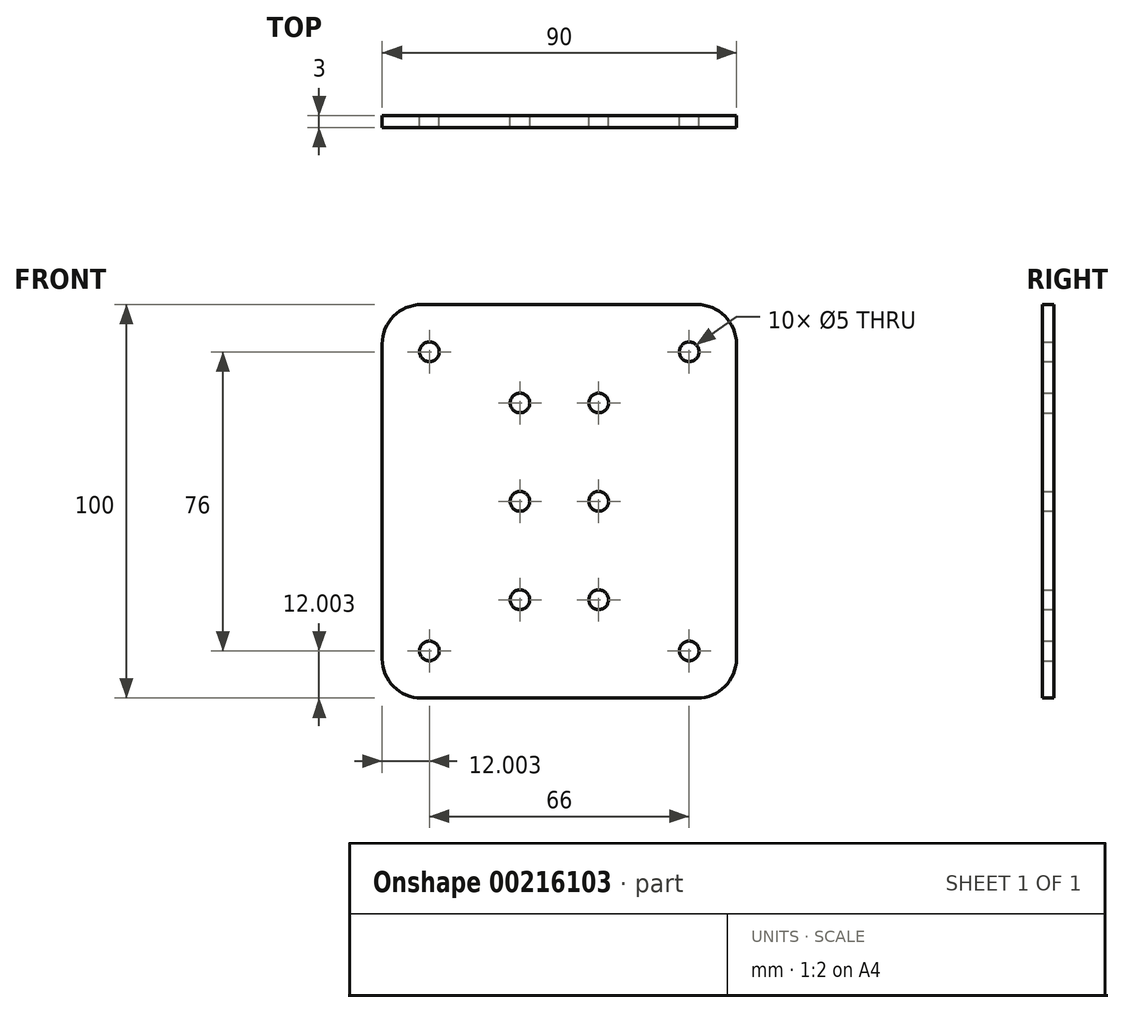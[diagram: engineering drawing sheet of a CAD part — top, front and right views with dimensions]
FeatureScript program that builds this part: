
annotation { "Feature Type Name" : "Feature", "Feature Type Description" : "" }
export const myFeature = defineFeature(function(context is Context, id is Id, definition is map)
    precondition{}
    {
        {
            var Q0;
            Q0=qCreatedBy(makeId("Front.planeOp"),FACE);
            var sketch = newSketch(context, id + "F0", { "sketchPlane" : qUnion([Q0])});
            skLineSegment(sketch, "E0.bottom", {"start": v(-55.35, 70.45) * mm, "end": v(34.65, 70.45) * mm});
            skLineSegment(sketch, "E0.top", {"start": v(-55.35, -29.55) * mm, "end": v(34.65, -29.55) * mm});
            skLineSegment(sketch, "E0.left", {"start": v(-55.35, 70.45) * mm, "end": v(-55.35, -29.55) * mm});
            skLineSegment(sketch, "E0.right", {"start": v(34.65, 70.45) * mm, "end": v(34.65, -29.55) * mm});
            skCircle(sketch, "E1", {"center": v(-43.35, 58.45) * mm, "radius": 2.5 * mm});
            skCircle(sketch, "E2", {"center": v(22.65, 58.45) * mm, "radius": 2.5 * mm});
            skCircle(sketch, "E3", {"center": v(22.65, -17.55) * mm, "radius": 2.5 * mm});
            skCircle(sketch, "E4", {"center": v(-43.35, -17.55) * mm, "radius": 2.5 * mm});
            skCircle(sketch, "E5", {"center": v(-20.35, -4.55) * mm, "radius": 2.5 * mm});
            skCircle(sketch, "E6", {"center": v(-0.35, -4.55) * mm, "radius": 2.5 * mm});
            skCircle(sketch, "E7", {"center": v(-0.35, 20.45) * mm, "radius": 2.5 * mm});
            skCircle(sketch, "E8", {"center": v(-20.35, 20.45) * mm, "radius": 2.5 * mm});
            skCircle(sketch, "E9", {"center": v(-0.35, 45.45) * mm, "radius": 2.5 * mm});
            skCircle(sketch, "E10", {"center": v(-20.35, 45.45) * mm, "radius": 2.5 * mm});
            skLineSegment(sketch, "E11.bottom", {"start": v(-20.35, 45.45) * mm, "end": v(-0.35, 45.45) * mm, "construction": true});
            skLineSegment(sketch, "E11.top", {"start": v(-20.35, -4.55) * mm, "end": v(-0.35, -4.55) * mm, "construction": true});
            skLineSegment(sketch, "E11.left", {"start": v(-20.35, 45.45) * mm, "end": v(-20.35, -4.55) * mm, "construction": true});
            skLineSegment(sketch, "E11.right", {"start": v(-0.35, 45.45) * mm, "end": v(-0.35, -4.55) * mm, "construction": true});
            skSolve(sketch);
        }
        {
            var Q0;
            Q0=makeQuery(id+"F0.imprint","IMPRINT",FACE,{"disambiguationData":[TD([[makeQuery(id+"F0.imprint","IMPRINT",EDGE,{"derivedFrom":sQuery(id+"F0.wireOp",EDGE,"E0.bottom")}),-1.0]])]});
            extrude(context, id + "F1", {"entities" : qUnion([Q0]), "depth" : 3 * mm});
        }
        {
            var Q0;
            Q0=makeQuery(id+"F1.opExtrude","SWEPT_EDGE",EDGE,{"disambiguationData":[OSD([sQuery(id+"F0.wireOp",EDGE,"E0.bottom"),sQuery(id+"F0.wireOp",EDGE,"E0.right")])]});
            var Q1;
            Q1=makeQuery(id+"F1.opExtrude","SWEPT_EDGE",EDGE,{"disambiguationData":[OSD([sQuery(id+"F0.wireOp",EDGE,"E0.bottom"),sQuery(id+"F0.wireOp",EDGE,"E0.left")])]});
            var Q2;
            Q2=makeQuery(id+"F1.opExtrude","SWEPT_EDGE",EDGE,{"disambiguationData":[OSD([sQuery(id+"F0.wireOp",EDGE,"E0.top"),sQuery(id+"F0.wireOp",EDGE,"E0.left")])]});
            var Q3;
            Q3=makeQuery(id+"F1.opExtrude","SWEPT_EDGE",EDGE,{"disambiguationData":[OSD([sQuery(id+"F0.wireOp",EDGE,"E0.top"),sQuery(id+"F0.wireOp",EDGE,"E0.right")])]});
            fillet(context, id + "F2", {"entities" : qUnion([Q0, Q1, Q2, Q3]), "radius" : 10 * mm, "tangentPropagation" : true, "allowEdgeOverflow" : false});
        }
    });
